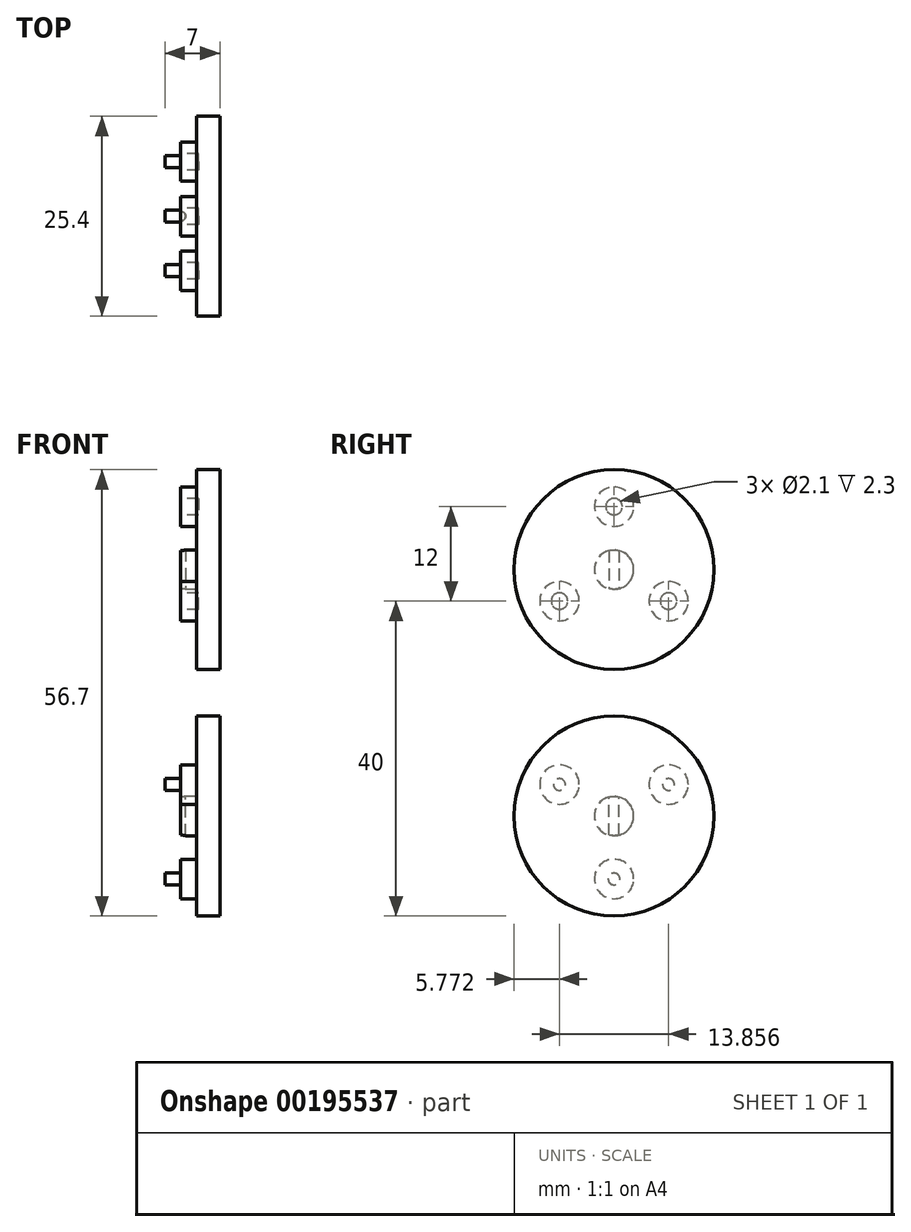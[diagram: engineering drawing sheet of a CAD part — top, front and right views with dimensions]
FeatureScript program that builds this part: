
annotation { "Feature Type Name" : "Feature", "Feature Type Description" : "" }
export const myFeature = defineFeature(function(context is Context, id is Id, definition is map)
    precondition{}
    {
        {
            var Q0;
            Q0=qCreatedBy(makeId("Right.planeOp"),FACE);
            var sketch = newSketch(context, id + "F0", { "sketchPlane" : qUnion([Q0])});
            skCircle(sketch, "E0", {"center": v(0, 0) * mm, "radius": 12.7 * mm});
            skSolve(sketch);
        }
        {
            var Q0;
            Q0=makeQuery(id+"F0.imprint","IMPRINT",FACE,{"disambiguationData":[TD([[makeQuery(id+"F0.imprint","IMPRINT",EDGE,{"derivedFrom":sQuery(id+"F0.wireOp",EDGE,"E0")}),1.0]])]});
            extrude(context, id + "F1", {"entities" : qUnion([Q0]), "depth" : 5 * mm});
        }
        {
            var Q0;
            Q0=makeQuery(id+"F1.opExtrude","CAP_FACE",FACE,{"disambiguationData":[OSD([sQuery(id+"F0.wireOp",EDGE,"E0")])],"isStart":true});
            var sketch = newSketch(context, id + "F2", { "sketchPlane" : qUnion([Q0])});
            skCircle(sketch, "E1", {"center": v(0, 0) * mm, "radius": 2.5 * mm});
            skCircle(sketch, "E2", {"center": v(0, -8) * mm, "radius": 2.5 * mm});
            skLineSegment(sketch, "E3", {"start": v(0, 0) * mm, "end": v(0, -8) * mm, "construction": true});
            skCircle(sketch, "E4", {"center": v(0, -8) * mm, "radius": 0.75 * mm});
            skCircle(sketch, "E5.1.0", {"center": v(6.93, 4) * mm, "radius": 2.5 * mm});
            skCircle(sketch, "E5.1.1", {"center": v(6.93, 4) * mm, "radius": 0.75 * mm});
            skCircle(sketch, "E5.2.0", {"center": v(-6.93, 4) * mm, "radius": 2.5 * mm});
            skCircle(sketch, "E5.2.1", {"center": v(-6.93, 4) * mm, "radius": 0.75 * mm});
            skSolve(sketch);
        }
        {
            var Q0;
            Q0=makeQuery(id+"F2.imprint","IMPRINT",FACE,{"disambiguationData":[TD([[makeQuery(id+"F2.imprint","IMPRINT",EDGE,{"derivedFrom":sQuery(id+"F2.wireOp",EDGE,"E1")}),-1.0]])]});
            extrude(context, id + "F3", {"entities" : qUnion([Q0]), "operationType" : NewBodyOperationType.REMOVE, "oppositeDirection" : true, "depth" : 2 * mm});
        }
        {
            var Q0;
            Q0=makeQuery(id+"F2.imprint","IMPRINT",FACE,{"disambiguationData":[TD([[makeQuery(id+"F2.imprint","IMPRINT",EDGE,{"derivedFrom":sQuery(id+"F2.wireOp",EDGE,"E5.1.1")}),1.0]])]});
            var Q1;
            Q1=makeQuery(id+"F2.imprint","IMPRINT",FACE,{"disambiguationData":[TD([[makeQuery(id+"F2.imprint","IMPRINT",EDGE,{"derivedFrom":sQuery(id+"F2.wireOp",EDGE,"E5.2.1")}),1.0]])]});
            var Q2;
            Q2=makeQuery(id+"F2.imprint","IMPRINT",FACE,{"disambiguationData":[TD([[makeQuery(id+"F2.imprint","IMPRINT",EDGE,{"derivedFrom":sQuery(id+"F2.wireOp",EDGE,"E4")}),1.0]])]});
            extrude(context, id + "F4", {"entities" : qUnion([Q0, Q1, Q2]), "operationType" : NewBodyOperationType.ADD, "depth" : 2 * mm});
        }
        {
            var Q0;
            Q0=makeQuery(id+"F3.boolean.opBoolean","SPLIT",FACE,{"disambiguationData":[TD([makeQuery(id+"F3.opExtrude","SWEPT_FACE",FACE,{"disambiguationData":[OSD([sQuery(id+"F2.wireOp",EDGE,"E1")])]})])],"derivedFrom":makeQuery(id+"F1.opExtrude","CAP_FACE",FACE,{"disambiguationData":[OSD([sQuery(id+"F0.wireOp",EDGE,"E0")])],"isStart":true})});
            var sketch = newSketch(context, id + "F5", { "sketchPlane" : qUnion([Q0])});
            skLineSegment(sketch, "E6", {"start": v(0, 0) * mm, "end": v(0, 2.5) * mm, "construction": true});
            skLineSegment(sketch, "E7.left", {"start": v(0.63, 2.5) * mm, "end": v(0.64, -2.5) * mm});
            skPoint(sketch, "E7.middle", {"position": v(0, 0) * mm});
            skLineSegment(sketch, "E8", {"start": v(0, 2.5) * mm, "end": v(0.64, 2.5) * mm});
            skLineSegment(sketch, "E9", {"start": v(0.64, -2.5) * mm, "end": v(0, -2.5) * mm});
            skLineSegment(sketch, "E10", {"start": v(0, -2.5) * mm, "end": v(0, 2.5) * mm});
            skSolve(sketch);
        }
        {
            var Q0;
            Q0 = qSketchRegion(id + "F5", true);
            var Q1;
            Q1=sQuery(id+"F5.wireOp",EDGE,"E10");
            revolve(context, id + "F6", {"operationType" : NewBodyOperationType.REMOVE, "entities" : qUnion([Q0]), "axis" : qUnion([Q1]), "revolveType" : RevolveType.FULL, "oppositeDirection" : true});
        }
        {
            var Q0;
            Q0=makeQuery(id+"F1.opExtrude","SWEPT_BODY",BODY,{"disambiguationData":[OSD([sQuery(id+"F0.wireOp",EDGE,"E0")])]});
            transform(context, id + "F7", {"entities" : qUnion([Q0]), "transformType" : TransformType.TRANSLATION_3D, "dx" : -15 * mm, "dy" : 0 * mm, "dz" : 0 * mm, "makeCopy" : true});
        }
        {
            var Q0;
            Q0=makeQuery(id+"F7.opPattern","COPY",FACE,{"derivedFrom":makeQuery(id+"F3.boolean.opBoolean","SPLIT",FACE,{"disambiguationData":[TD([makeQuery(id+"F3.opExtrude","SWEPT_FACE",FACE,{"disambiguationData":[OSD([sQuery(id+"F2.wireOp",EDGE,"E1")])]})])],"derivedFrom":makeQuery(id+"F1.opExtrude","CAP_FACE",FACE,{"disambiguationData":[OSD([sQuery(id+"F0.wireOp",EDGE,"E0")])],"isStart":true})}),"instanceName":"1"});
            var sketch = newSketch(context, id + "F8", { "sketchPlane" : qUnion([Q0])});
            skLineSegment(sketch, "E11", {"start": v(0, 0) * mm, "end": v(-21.29, 0) * mm, "construction": true});
            skSolve(sketch);
        }
        {
            var Q0;
            Q0=makeQuery(id+"F7.opPattern","COPY",BODY,{"derivedFrom":makeQuery(id+"F1.opExtrude","SWEPT_BODY",BODY,{"disambiguationData":[OSD([sQuery(id+"F0.wireOp",EDGE,"E0")])]}),"instanceName":"1"});
            var Q1;
            Q1=sQuery(id+"F8.wireOp",EDGE,"E11");
            transform(context, id + "F9", {"entities" : qUnion([Q0]), "transformType" : TransformType.ROTATION, "transformAxis" : qUnion([Q1]), "angle" : 180 * degree, "makeCopy" : false});
        }
        {
            var Q0;
            Q0=qCreatedBy(makeId("Front.planeOp"),FACE);
            var sketch = newSketch(context, id + "F10", { "sketchPlane" : qUnion([Q0])});
            skLineSegment(sketch, "E12", {"start": v(0, 0) * mm, "end": v(-15, 0) * mm, "construction": true});
            skSolve(sketch);
        }
        {
            var Q0;
            Q0=makeQuery(id+"F7.opPattern","COPY",BODY,{"derivedFrom":makeQuery(id+"F1.opExtrude","SWEPT_BODY",BODY,{"disambiguationData":[OSD([sQuery(id+"F0.wireOp",EDGE,"E0")])]}),"instanceName":"1"});
            var Q1;
            Q1=sQuery(id+"F10.wireOp",EDGE,"E12");
            transform(context, id + "F11", {"entities" : qUnion([Q0]), "transformType" : TransformType.ROTATION, "transformAxis" : qUnion([Q1]), "angle" : 180 * degree, "makeCopy" : false});
        }
        {
            var Q0;
            Q0=makeQuery(id+"F7.opPattern","COPY",BODY,{"derivedFrom":makeQuery(id+"F1.opExtrude","SWEPT_BODY",BODY,{"disambiguationData":[OSD([sQuery(id+"F0.wireOp",EDGE,"E0")])]}),"instanceName":"1"});
            var Q1;
            Q1=sQuery(id+"F10.wireOp",EDGE,"E12");
            transform(context, id + "F12", {"entities" : qUnion([Q0]), "transformType" : TransformType.TRANSLATION_ENTITY, "oppositeDirectionEntity" : true, "transformLine" : qUnion([Q1]), "makeCopy" : false});
        }
        {
            var Q0;
            Q0=makeQuery(id+"F1.opExtrude","SWEPT_BODY",BODY,{"disambiguationData":[OSD([sQuery(id+"F0.wireOp",EDGE,"E0")])]});
            var Q1;
            Q1=makeQuery(id+"F7.opPattern","COPY",BODY,{"derivedFrom":makeQuery(id+"F1.opExtrude","SWEPT_BODY",BODY,{"disambiguationData":[OSD([sQuery(id+"F0.wireOp",EDGE,"E0")])]}),"instanceName":"1"});
            var Q2;
            Q2=makeQuery(id+"F4.opExtrude","SWEPT_FACE",FACE,{"disambiguationData":[OSD([sQuery(id+"F2.wireOp",EDGE,"E5.2.1")])]});
            var Q3;
            Q3=makeQuery(id+"F4.opExtrude","SWEPT_FACE",FACE,{"disambiguationData":[OSD([sQuery(id+"F2.wireOp",EDGE,"E4")])]});
            var Q4;
            Q4=makeQuery(id+"F4.opExtrude","SWEPT_FACE",FACE,{"disambiguationData":[OSD([sQuery(id+"F2.wireOp",EDGE,"E5.1.1")])]});
            var Q5;
            Q5=makeQuery(id+"F4.opExtrude","CAP_FACE",FACE,{"disambiguationData":[OSD([sQuery(id+"F2.wireOp",EDGE,"E5.2.1")])],"isStart":false});
            var Q6;
            Q6=makeQuery(id+"F4.opExtrude","CAP_FACE",FACE,{"disambiguationData":[OSD([sQuery(id+"F2.wireOp",EDGE,"E5.1.1")])],"isStart":false});
            var Q7;
            Q7=makeQuery(id+"F4.opExtrude","CAP_FACE",FACE,{"disambiguationData":[OSD([sQuery(id+"F2.wireOp",EDGE,"E4")])],"isStart":false});
            booleanBodies(context, id + "F13", {"operationType" : BooleanOperationType.SUBTRACTION, "tools" : qUnion([Q0]), "targets" : qUnion([Q1]), "offset" : true, "entitiesToOffset" : qUnion([Q2, Q3, Q4, Q5, Q6, Q7]), "offsetDistance" : .3 * mm, "keepTools" : true});
        }
        {
            var Q0;
            Q0=makeQuery(id+"F7.opPattern","COPY",BODY,{"derivedFrom":makeQuery(id+"F1.opExtrude","SWEPT_BODY",BODY,{"disambiguationData":[OSD([sQuery(id+"F0.wireOp",EDGE,"E0")])]}),"instanceName":"1"});
            var Q1;
            Q1=sQuery(id+"F10.wireOp",EDGE,"E12");
            transform(context, id + "F14", {"entities" : qUnion([Q0]), "transformType" : TransformType.TRANSLATION_ENTITY, "oppositeDirectionEntity" : false, "transformLine" : qUnion([Q1]), "makeCopy" : false});
        }
        {
            var Q0;
            Q0=qCreatedBy(makeId("Top.planeOp"),FACE);
            var sketch = newSketch(context, id + "F15", { "sketchPlane" : qUnion([Q0])});
            skPoint(sketch, "E13", {"position": v(-7.5, 0) * mm});
            skLineSegment(sketch, "E14", {"start": v(-7.5, 0) * mm, "end": v(-7.5, -10.4) * mm, "construction": true});
            skSolve(sketch);
        }
        {
            var Q0;
            Q0=makeQuery(id+"F7.opPattern","COPY",BODY,{"derivedFrom":makeQuery(id+"F1.opExtrude","SWEPT_BODY",BODY,{"disambiguationData":[OSD([sQuery(id+"F0.wireOp",EDGE,"E0")])]}),"instanceName":"1"});
            var Q1;
            Q1=sQuery(id+"F15.wireOp",EDGE,"E14");
            transform(context, id + "F16", {"entities" : qUnion([Q0]), "transformType" : TransformType.ROTATION, "transformAxis" : qUnion([Q1]), "angle" : 180 * degree, "makeCopy" : false});
        }
        {
            var Q0;
            Q0=makeQuery(id+"F7.opPattern","COPY",BODY,{"derivedFrom":makeQuery(id+"F1.opExtrude","SWEPT_BODY",BODY,{"disambiguationData":[OSD([sQuery(id+"F0.wireOp",EDGE,"E0")])]}),"instanceName":"1"});
            transform(context, id + "F17", {"entities" : qUnion([Q0]), "transformType" : TransformType.TRANSLATION_3D, "dx" : 0 * mm, "dy" : 0 * mm, "dz" : 31.3 * mm, "makeCopy" : false});
        }
    });
